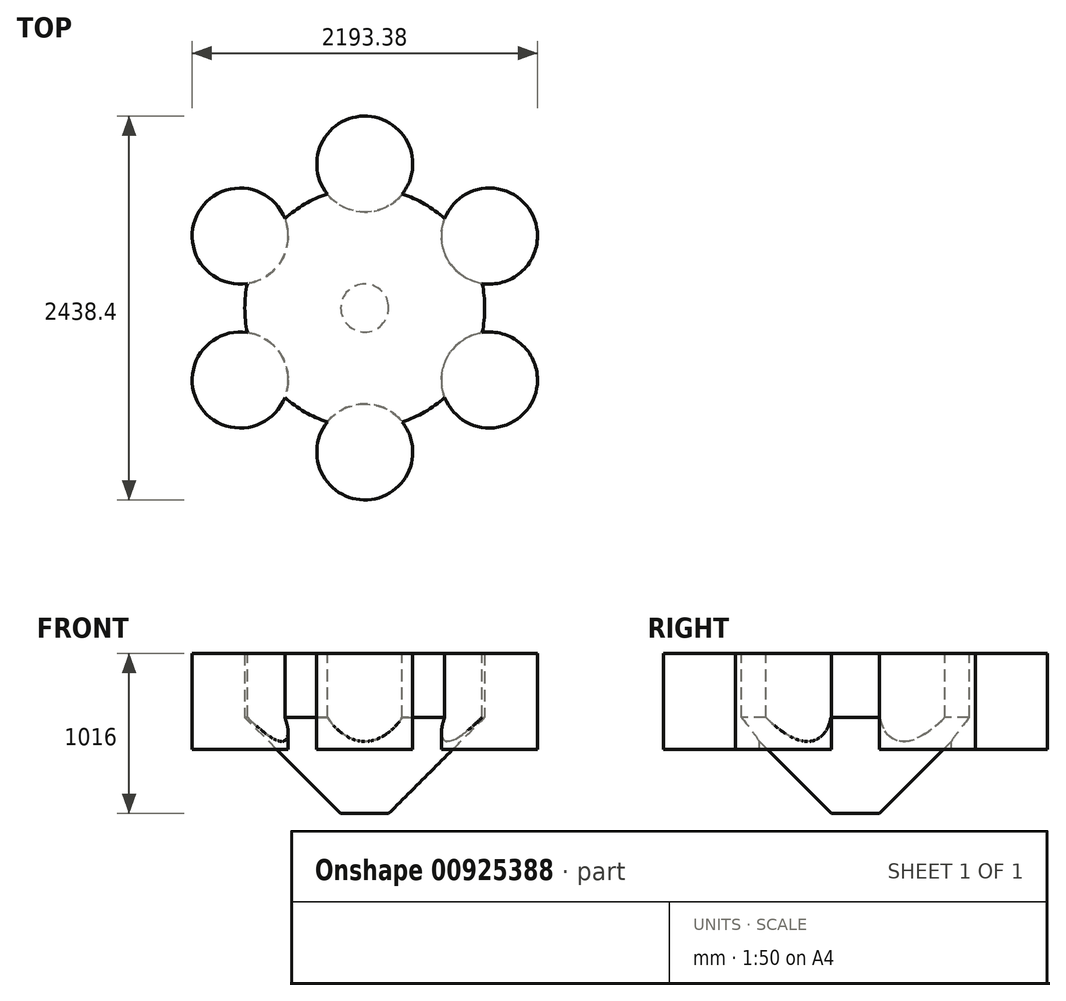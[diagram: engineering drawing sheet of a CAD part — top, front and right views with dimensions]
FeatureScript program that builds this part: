
annotation { "Feature Type Name" : "Feature", "Feature Type Description" : "" }
export const myFeature = defineFeature(function(context is Context, id is Id, definition is map)
    precondition{}
    {
        {
            var Q0;
            Q0=qCreatedBy(makeId("Top.planeOp"),FACE);
            var sketch = newSketch(context, id + "F0", { "sketchPlane" : qUnion([Q0])});
            skCircle(sketch, "E0", {"center": v(0, 0) * mm, "radius": 762 * mm});
            skSolve(sketch);
        }
        {
            var Q0;
            Q0 = qSketchRegion(id + "F0", true);
            extrude(context, id + "F1", {"entities" : qUnion([Q0]), "depth" : 1016 * mm, "offsetDistance" : 25.4 * mm});
        }
        {
            var Q0;
            Q0=makeQuery(id+"F1.opExtrude","CAP_EDGE",EDGE,{"disambiguationData":[OSD([sQuery(id+"F0.wireOp",EDGE,"E0")])],"isStart":true});
            chamfer(context, id + "F2", {"entities" : qUnion([Q0]), "width" : 609.6 * mm, "tangentPropagation" : true});
        }
        {
            var Q0;
            Q0=makeQuery(id+"F1.opExtrude","CAP_FACE",FACE,{"disambiguationData":[OSD([sQuery(id+"F0.wireOp",EDGE,"E0")])],"isStart":false});
            var sketch = newSketch(context, id + "F3", { "sketchPlane" : qUnion([Q0])});
            skCircle(sketch, "E1", {"center": v(0, 914.4) * mm, "radius": 304.8 * mm});
            skLineSegment(sketch, "E2", {"start": v(0, 0) * mm, "end": v(0, 914.4) * mm, "construction": true});
            skCircle(sketch, "E3.1.0", {"center": v(791.9, 457.2) * mm, "radius": 304.8 * mm});
            skCircle(sketch, "E3.2.0", {"center": v(791.9, -457.2) * mm, "radius": 304.8 * mm});
            skCircle(sketch, "E3.3.0", {"center": v(0, -914.4) * mm, "radius": 304.8 * mm});
            skCircle(sketch, "E3.4.0", {"center": v(-791.9, -457.2) * mm, "radius": 304.8 * mm});
            skCircle(sketch, "E3.5.0", {"center": v(-791.9, 457.2) * mm, "radius": 304.8 * mm});
            skPoint(sketch, "E3.center", {"position": v(0, 0) * mm});
            skLineSegment(sketch, "E3.anchor2", {"start": v(0, 0) * mm, "end": v(-791.9, 457.2) * mm, "construction": true});
            skSolve(sketch);
        }
        {
            var Q0;
            Q0 = qSketchRegion(id + "F3", true);
            extrude(context, id + "F4", {"entities" : qUnion([Q0]), "operationType" : NewBodyOperationType.ADD, "oppositeDirection" : true, "depth" : 609.6 * mm, "offsetDistance" : 25.4 * mm});
        }
    });
